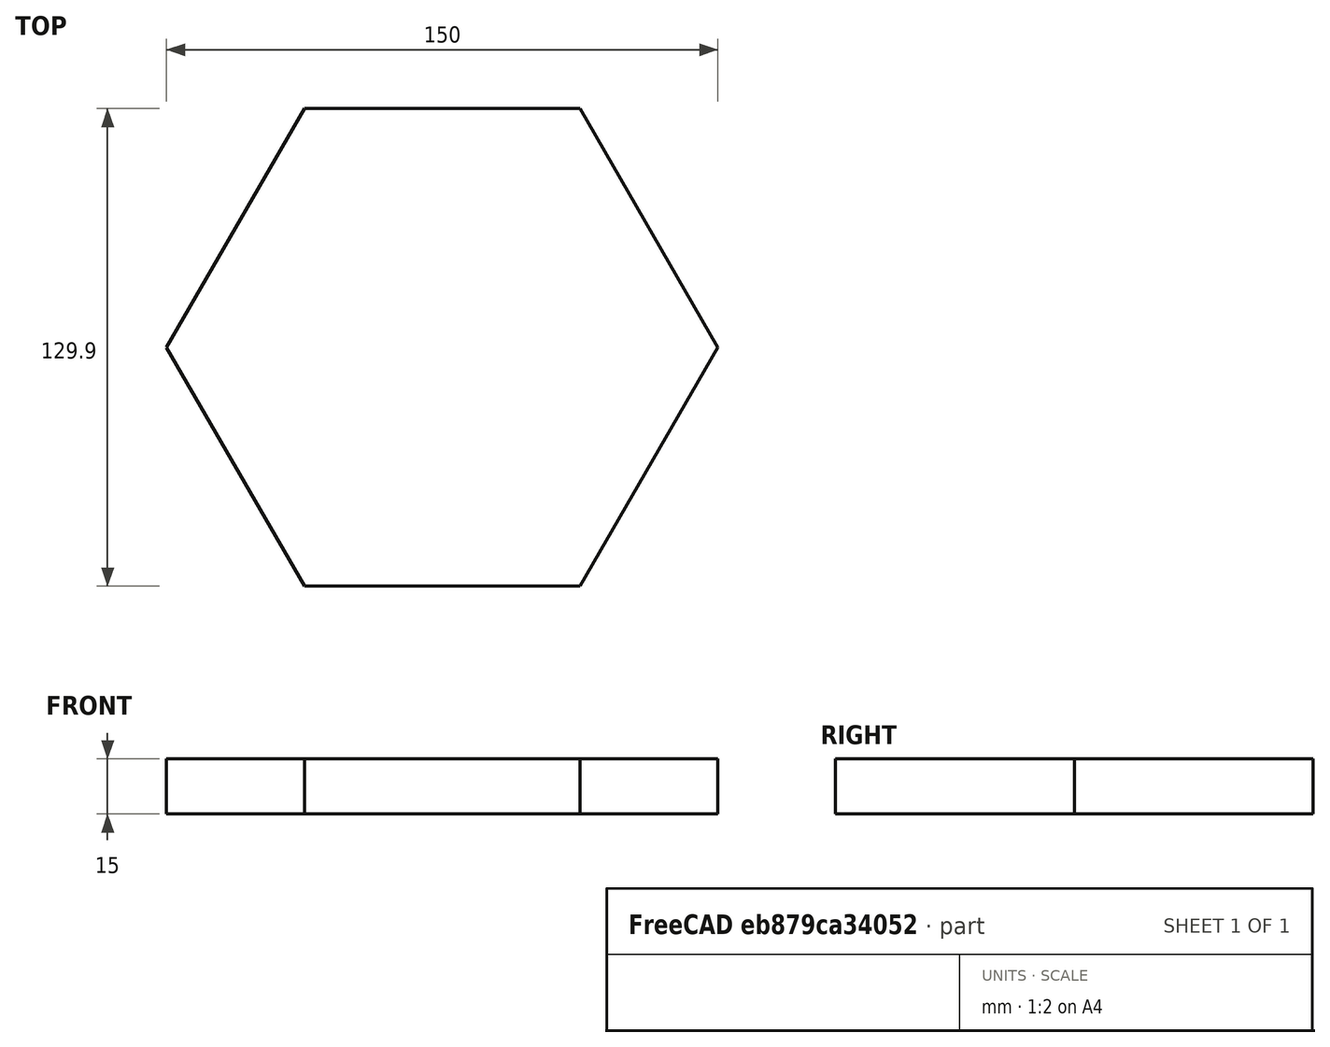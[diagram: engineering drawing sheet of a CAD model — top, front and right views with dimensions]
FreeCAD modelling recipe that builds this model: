
FCSTD DOCUMENT  (FreeCAD 0.19R24291 (Git))
Label: Echantillon
License: All rights reserved
LicenseURL: http://en.wikipedia.org/wiki/All_rights_reserved
objects: Sketcher::SketchObject×1, PartDesign::Pad×1, PartDesign::Body×1
note: 4 computed .brp shape members not serialized (recipe doc carries the construction recipe); baked Part::Feature solids carry a one-line shape summary decoded from their .brp

FEATURE [Sketcher::SketchObject] Sketch  label="sk1"
  FullyConstrained = true
  MapMode = 5
  Support = -> [XY_Plane]
  sketch-geometry (7):
    g0: LineSegment StartX=-37.5 StartY=64.9519 StartZ=0 EndX=-75 EndY=0 EndZ=0
    g1: LineSegment StartX=-75 StartY=1e-16 StartZ=0 EndX=-37.5 EndY=-64.9519 EndZ=0
    g2: LineSegment StartX=-37.5 StartY=-64.9519 StartZ=0 EndX=37.5 EndY=-64.9519 EndZ=0
    g3: LineSegment StartX=37.5 StartY=-64.9519 StartZ=0 EndX=75 EndY=1.42e-14 EndZ=0
    g4: LineSegment StartX=75 StartY=1.18e-14 StartZ=0 EndX=37.5 EndY=64.9519 EndZ=0
    g5: LineSegment StartX=37.5 StartY=64.9519 StartZ=0 EndX=-37.5 EndY=64.9519 EndZ=0
    g6: Circle CenterX=0 CenterY=0 CenterZ=0 NormalX=0 NormalY=0 NormalZ=1 AngleXU=0 Radius=75
  constraints (16):
    c: Coincident(g0,g1)
    c: Coincident(g1,g2)
    c: Coincident(g2,g3)
    c: Coincident(g3,g4)
    c: Coincident(g4,g5)
    c: Coincident(g5,g0)
    c: Equal(g0, g1-g5) x5
    c: PointOnObject(g0,g6)
    c: PointOnObject(g1,g6)
    c: PointOnObject(g2,g6)
    c: PointOnObject(g3,g6)
    c: PointOnObject(g4,g6)
    c: PointOnObject(g5,g6)
    c: Coincident(g6,g-1)
    c: Parallel(g5,g-1)
    c: DistanceX(g0,g3) = 150
FEATURE [PartDesign::Pad] Pad  label="Echantillon"
  Direction = (1,1,1)
  Length = 15
  Length2 = 100
  Profile = -> Sketch
  Type = 0
FEATURE [PartDesign::Body] Body
  Group = -> [Sketch,Pad]
  Origin = -> Origin
  Tip = -> Pad
